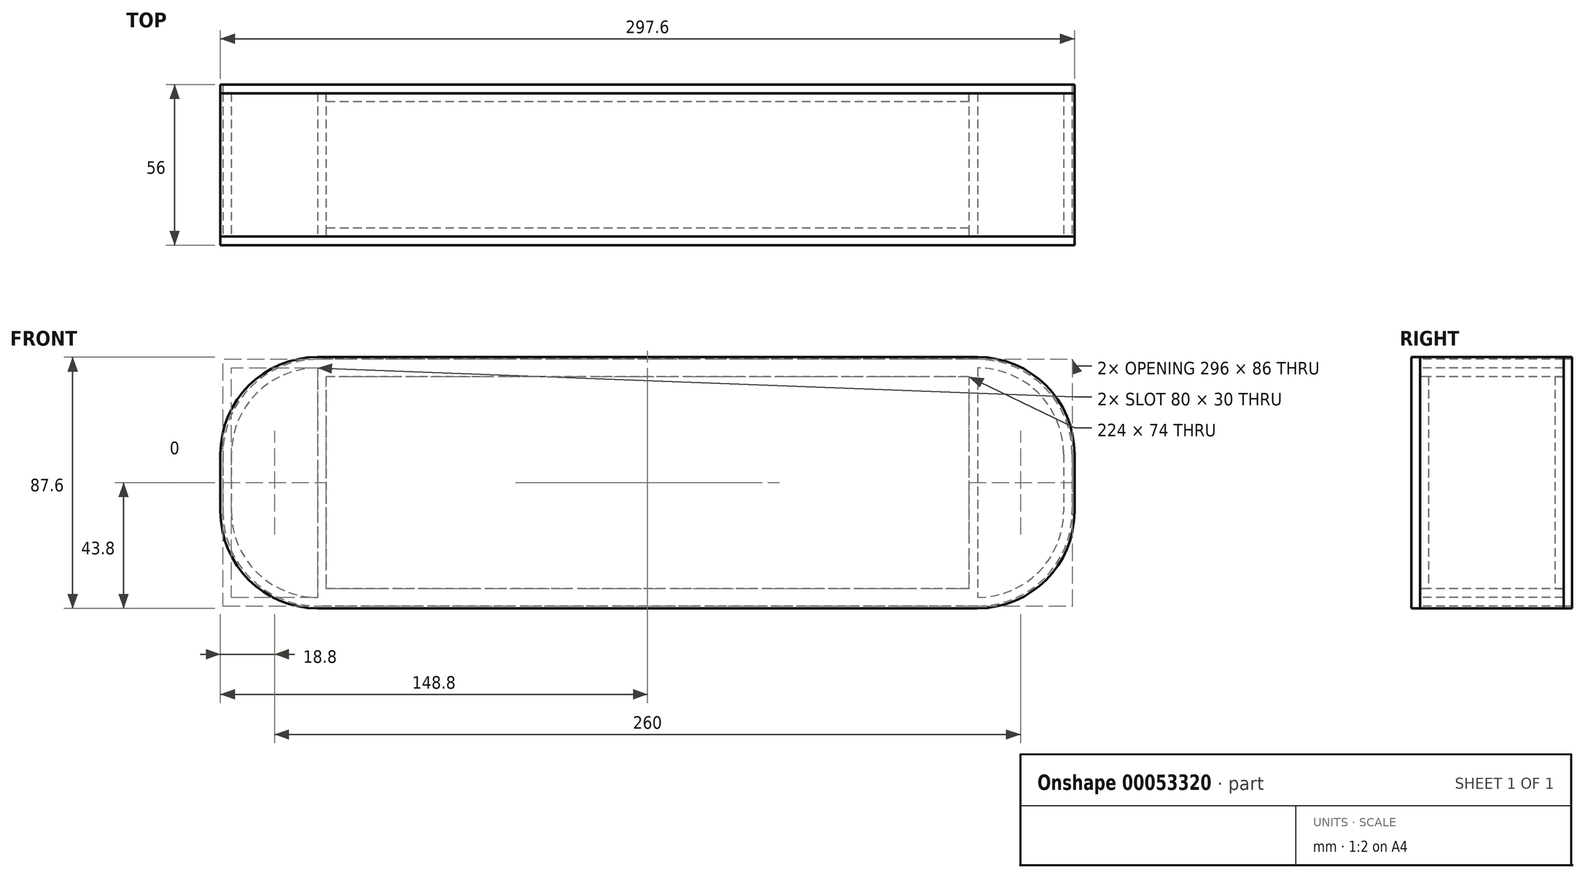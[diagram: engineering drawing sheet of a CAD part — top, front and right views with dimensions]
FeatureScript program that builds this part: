
annotation { "Feature Type Name" : "Feature", "Feature Type Description" : "" }
export const myFeature = defineFeature(function(context is Context, id is Id, definition is map)
    precondition{}
    {
        {
            var Q0;
            Q0=qCreatedBy(makeId("Front.planeOp"),FACE);
            var sketch = newSketch(context, id + "F0", { "sketchPlane" : qUnion([Q0])});
            skLineSegment(sketch, "E0.rect.bottom", {"start": v(115, 40) * mm, "end": v(-115, 40) * mm});
            skLineSegment(sketch, "E0.rect.top", {"start": v(115, -40) * mm, "end": v(-115, -40) * mm});
            skLineSegment(sketch, "E0.rect.left", {"start": v(145, 10) * mm, "end": v(145, -10) * mm});
            skLineSegment(sketch, "E0.rect.right", {"start": v(-145, 10) * mm, "end": v(-145, -10) * mm});
            skPoint(sketch, "E0.rect.middle", {"position": v(0, 0) * mm});
            skPoint(sketch, "E1.visualSharp", {"position": v(-145, 40) * mm});
            skArc(sketch, "E1.filletArc", {"start": v(-115, 40) * mm, "mid": v(-136.21, 31.21) * mm, "end": v(-145, 10) * mm});
            skPoint(sketch, "E2.visualSharp", {"position": v(145, 40) * mm});
            skArc(sketch, "E2.filletArc", {"start": v(145, 10) * mm, "mid": v(136.21, 31.21) * mm, "end": v(115, 40) * mm});
            skPoint(sketch, "E3.visualSharp", {"position": v(145, -40) * mm});
            skArc(sketch, "E3.filletArc", {"start": v(115, -40) * mm, "mid": v(136.21, -31.21) * mm, "end": v(145, -10) * mm});
            skPoint(sketch, "E4.visualSharp", {"position": v(-145, -40) * mm});
            skArc(sketch, "E4.filletArc", {"start": v(-145, -10) * mm, "mid": v(-136.21, -31.21) * mm, "end": v(-115, -40) * mm});
            skLineSegment(sketch, "E5.0", {"start": v(-148, 10) * mm, "end": v(-148, -10) * mm});
            skArc(sketch, "E5.1", {"start": v(-115, 43) * mm, "mid": v(-138.33, 33.33) * mm, "end": v(-148, 10) * mm});
            skLineSegment(sketch, "E5.2", {"start": v(115, 43) * mm, "end": v(-115, 43) * mm});
            skArc(sketch, "E6.0", {"start": v(148, 10) * mm, "mid": v(138.33, 33.33) * mm, "end": v(115, 43) * mm});
            skArc(sketch, "E6.1", {"start": v(-148, -10) * mm, "mid": v(-138.33, -33.33) * mm, "end": v(-115, -43) * mm});
            skLineSegment(sketch, "E6.2", {"start": v(115, -43) * mm, "end": v(-115, -43) * mm});
            skArc(sketch, "E6.3", {"start": v(115, -43) * mm, "mid": v(138.33, -33.33) * mm, "end": v(148, -10) * mm});
            skLineSegment(sketch, "E6.4", {"start": v(148, 10) * mm, "end": v(148, -10) * mm});
            skLineSegment(sketch, "E7.0", {"start": v(115, 43.8) * mm, "end": v(-115, 43.8) * mm});
            skArc(sketch, "E7.1", {"start": v(148.8, 10) * mm, "mid": v(138.9, 33.9) * mm, "end": v(115, 43.8) * mm});
            skArc(sketch, "E7.2", {"start": v(-115, 43.8) * mm, "mid": v(-138.9, 33.9) * mm, "end": v(-148.8, 10) * mm});
            skLineSegment(sketch, "E7.3", {"start": v(148.8, 10) * mm, "end": v(148.8, -10) * mm});
            skLineSegment(sketch, "E7.4", {"start": v(-148.8, 10) * mm, "end": v(-148.8, -10) * mm});
            skArc(sketch, "E7.5", {"start": v(-148.8, -10) * mm, "mid": v(-138.9, -33.9) * mm, "end": v(-115, -43.8) * mm});
            skLineSegment(sketch, "E7.6", {"start": v(115, -43.8) * mm, "end": v(-115, -43.8) * mm});
            skArc(sketch, "E7.7", {"start": v(115, -43.8) * mm, "mid": v(138.9, -33.9) * mm, "end": v(148.8, -10) * mm});
            skLineSegment(sketch, "E8.left", {"start": v(115, 40) * mm, "end": v(115, -40) * mm});
            skLineSegment(sketch, "E8.right", {"start": v(-115, 40) * mm, "end": v(-115, -40) * mm});
            skLineSegment(sketch, "E9.0", {"start": v(112, 37) * mm, "end": v(-112, 37) * mm});
            skLineSegment(sketch, "E9.1", {"start": v(112, 37) * mm, "end": v(112, -37) * mm});
            skLineSegment(sketch, "E9.2", {"start": v(112, -37) * mm, "end": v(-112, -37) * mm});
            skLineSegment(sketch, "E9.3", {"start": v(-112, 37) * mm, "end": v(-112, -37) * mm});
            skSolve(sketch);
        }
        {
            var Q0;
            Q0=makeQuery(id+"F0.imprint","IMPRINT",FACE,{"disambiguationData":[TD([[makeQuery(id+"F0.imprint","IMPRINT",EDGE,{"derivedFrom":sQuery(id+"F0.wireOp",EDGE,"E0.rect.bottom")}),1.0]])]});
            var Q1;
            Q1=makeQuery(id+"F0.imprint","IMPRINT",FACE,{"disambiguationData":[TD([[makeQuery(id+"F0.imprint","IMPRINT",EDGE,{"derivedFrom":sQuery(id+"F0.wireOp",EDGE,"E0.rect.left")}),1.0]])]});
            extrude(context, id + "F1", {"entities" : qUnion([Q0, Q1]), "oppositeDirection" : true, "depth" : 50 * mm});
        }
        {
            var Q0;
            Q0=makeQuery(id+"F0.imprint","IMPRINT",FACE,{"disambiguationData":[TD([[makeQuery(id+"F0.imprint","IMPRINT",EDGE,{"derivedFrom":sQuery(id+"F0.wireOp",EDGE,"E9.0")}),1.0]])]});
            extrude(context, id + "F2", {"entities" : qUnion([Q0]), "oppositeDirection" : true, "depth" : 3 * mm});
        }
        {
            var Q0;
            Q0=makeQuery(id+"F0.imprint","IMPRINT",FACE,{"disambiguationData":[TD([[makeQuery(id+"F0.imprint","IMPRINT",EDGE,{"derivedFrom":sQuery(id+"F0.wireOp",EDGE,"E5.0")}),-1.0]])]});
            var Q1;
            Q1=makeQuery(id+"F0.imprint","IMPRINT",FACE,{"disambiguationData":[TD([[makeQuery(id+"F0.imprint","IMPRINT",EDGE,{"derivedFrom":sQuery(id+"F0.wireOp",EDGE,"E0.rect.left")}),1.0]])]});
            var Q2;
            Q2=makeQuery(id+"F0.imprint","IMPRINT",FACE,{"disambiguationData":[TD([[makeQuery(id+"F0.imprint","IMPRINT",EDGE,{"derivedFrom":sQuery(id+"F0.wireOp",EDGE,"E0.rect.bottom")}),1.0]])]});
            var Q3;
            Q3=makeQuery(id+"F0.imprint","IMPRINT",FACE,{"disambiguationData":[TD([[makeQuery(id+"F0.imprint","IMPRINT",EDGE,{"derivedFrom":sQuery(id+"F0.wireOp",EDGE,"E9.0")}),1.0]])]});
            var Q4;
            Q4=makeQuery(id+"F0.imprint","IMPRINT",FACE,{"disambiguationData":[TD([[makeQuery(id+"F0.imprint","IMPRINT",EDGE,{"derivedFrom":sQuery(id+"F0.wireOp",EDGE,"E0.rect.right")}),1.0]])]});
            var Q5;
            Q5=makeQuery(id+"F0.imprint","IMPRINT",FACE,{"disambiguationData":[TD([[makeQuery(id+"F0.imprint","IMPRINT",EDGE,{"derivedFrom":sQuery(id+"F0.wireOp",EDGE,"E0.rect.left")}),-1.0]])]});
            extrude(context, id + "F3", {"entities" : qUnion([Q0, Q1, Q2, Q3, Q4, Q5]), "depth" : 3 * mm});
        }
        {
            var Q0;
            Q0=makeQuery(id+"F0.imprint","IMPRINT",FACE,{"disambiguationData":[TD([[makeQuery(id+"F0.imprint","IMPRINT",EDGE,{"derivedFrom":sQuery(id+"F0.wireOp",EDGE,"E5.0")}),-1.0]])]});
            extrude(context, id + "F4", {"entities" : qUnion([Q0]), "oppositeDirection" : true, "depth" : 50 * mm});
        }
        {
            var Q0;
            Q0=makeQuery(id+"F1.opExtrude","CAP_FACE",FACE,{"disambiguationData":[OSD([sQuery(id+"F0.wireOp",EDGE,"E0.rect.left"),sQuery(id+"F0.wireOp",EDGE,"E0.rect.right"),sQuery(id+"F0.wireOp",EDGE,"E1.filletArc"),sQuery(id+"F0.wireOp",EDGE,"E2.filletArc"),sQuery(id+"F0.wireOp",EDGE,"E3.filletArc"),sQuery(id+"F0.wireOp",EDGE,"E4.filletArc"),sQuery(id+"F0.wireOp",EDGE,"E5.0"),sQuery(id+"F0.wireOp",EDGE,"E5.1"),sQuery(id+"F0.wireOp",EDGE,"E5.2"),sQuery(id+"F0.wireOp",EDGE,"E6.0"),sQuery(id+"F0.wireOp",EDGE,"E6.1"),sQuery(id+"F0.wireOp",EDGE,"E6.2"),sQuery(id+"F0.wireOp",EDGE,"E6.3"),sQuery(id+"F0.wireOp",EDGE,"E6.4"),sQuery(id+"F0.wireOp",EDGE,"E8.left"),sQuery(id+"F0.wireOp",EDGE,"E8.right"),sQuery(id+"F0.wireOp",EDGE,"E9.0"),sQuery(id+"F0.wireOp",EDGE,"E9.1"),sQuery(id+"F0.wireOp",EDGE,"E9.2"),sQuery(id+"F0.wireOp",EDGE,"E9.3")])],"isStart":false});
            var sketch = newSketch(context, id + "F5", { "sketchPlane" : qUnion([Q0])});
            skArc(sketch, "E10.0", {"start": v(-145, 10) * mm, "mid": v(-136.21, 31.21) * mm, "end": v(-115, 40) * mm});
            skLineSegment(sketch, "E11.0", {"start": v(-145, 10) * mm, "end": v(-145, -10) * mm});
            skArc(sketch, "E12.0", {"start": v(-115, -40) * mm, "mid": v(-136.21, -31.21) * mm, "end": v(-145, -10) * mm});
            skLineSegment(sketch, "E13.0", {"start": v(-115, 40) * mm, "end": v(-115, -40) * mm});
            skLineSegment(sketch, "E14.0", {"start": v(115, 40) * mm, "end": v(115, -40) * mm});
            skArc(sketch, "E15.0", {"start": v(115, 40) * mm, "mid": v(136.21, 31.21) * mm, "end": v(145, 10) * mm});
            skLineSegment(sketch, "E16.0", {"start": v(145, 10) * mm, "end": v(145, -10) * mm});
            skArc(sketch, "E17.0", {"start": v(145, -10) * mm, "mid": v(136.21, -31.21) * mm, "end": v(115, -40) * mm});
            skSolve(sketch);
        }
        {
            var Q0;
            Q0=makeQuery(id+"F5.imprint","IMPRINT",FACE,{"disambiguationData":[TD([[makeQuery(id+"F5.imprint","IMPRINT",EDGE,{"derivedFrom":makeQuery(id+"F1.opExtrude","CAP_EDGE",EDGE,{"disambiguationData":[OSD([sQuery(id+"F0.wireOp",EDGE,"E9.0")])],"isStart":false})}),-1.0]])]});
            extrude(context, id + "F6", {"entities" : qUnion([Q0]), "oppositeDirection" : true, "depth" : 3 * mm});
        }
        {
            var Q0;
            Q0=makeQuery(id+"F5.imprint","IMPRINT",FACE,{"disambiguationData":[TD([[makeQuery(id+"F5.imprint","IMPRINT",EDGE,{"derivedFrom":sQuery(id+"F5.wireOp",EDGE,"E10.0")}),-1.0]])]});
            var Q1;
            Q1=makeQuery(id+"F5.imprint","IMPRINT",FACE,{"disambiguationData":[TD([[makeQuery(id+"F5.imprint","IMPRINT",EDGE,{"derivedFrom":sQuery(id+"F5.wireOp",EDGE,"E10.0")}),1.0]])]});
            var Q2;
            Q2=makeQuery(id+"F5.imprint","IMPRINT",FACE,{"disambiguationData":[TD([[makeQuery(id+"F5.imprint","IMPRINT",EDGE,{"derivedFrom":makeQuery(id+"F1.opExtrude","CAP_EDGE",EDGE,{"disambiguationData":[OSD([sQuery(id+"F0.wireOp",EDGE,"E9.0")])],"isStart":false})}),-1.0]])]});
            var Q3;
            Q3=makeQuery(id+"F4.opExtrude","CAP_FACE",FACE,{"disambiguationData":[OSD([sQuery(id+"F0.wireOp",EDGE,"E5.0"),sQuery(id+"F0.wireOp",EDGE,"E5.1"),sQuery(id+"F0.wireOp",EDGE,"E5.2"),sQuery(id+"F0.wireOp",EDGE,"E6.0"),sQuery(id+"F0.wireOp",EDGE,"E6.1"),sQuery(id+"F0.wireOp",EDGE,"E6.2"),sQuery(id+"F0.wireOp",EDGE,"E6.3"),sQuery(id+"F0.wireOp",EDGE,"E6.4"),sQuery(id+"F0.wireOp",EDGE,"E7.0"),sQuery(id+"F0.wireOp",EDGE,"E7.1"),sQuery(id+"F0.wireOp",EDGE,"E7.2"),sQuery(id+"F0.wireOp",EDGE,"E7.3"),sQuery(id+"F0.wireOp",EDGE,"E7.4"),sQuery(id+"F0.wireOp",EDGE,"E7.5"),sQuery(id+"F0.wireOp",EDGE,"E7.6"),sQuery(id+"F0.wireOp",EDGE,"E7.7")])],"isStart":false});
            var Q4;
            Q4=makeQuery(id+"F5.imprint","IMPRINT",FACE,{"disambiguationData":[TD([[makeQuery(id+"F5.imprint","IMPRINT",EDGE,{"derivedFrom":sQuery(id+"F5.wireOp",EDGE,"E14.0")}),1.0]])]});
            extrude(context, id + "F7", {"entities" : qUnion([Q0, Q1, Q2, Q3, Q4]), "depth" : 3 * mm});
        }
    });
